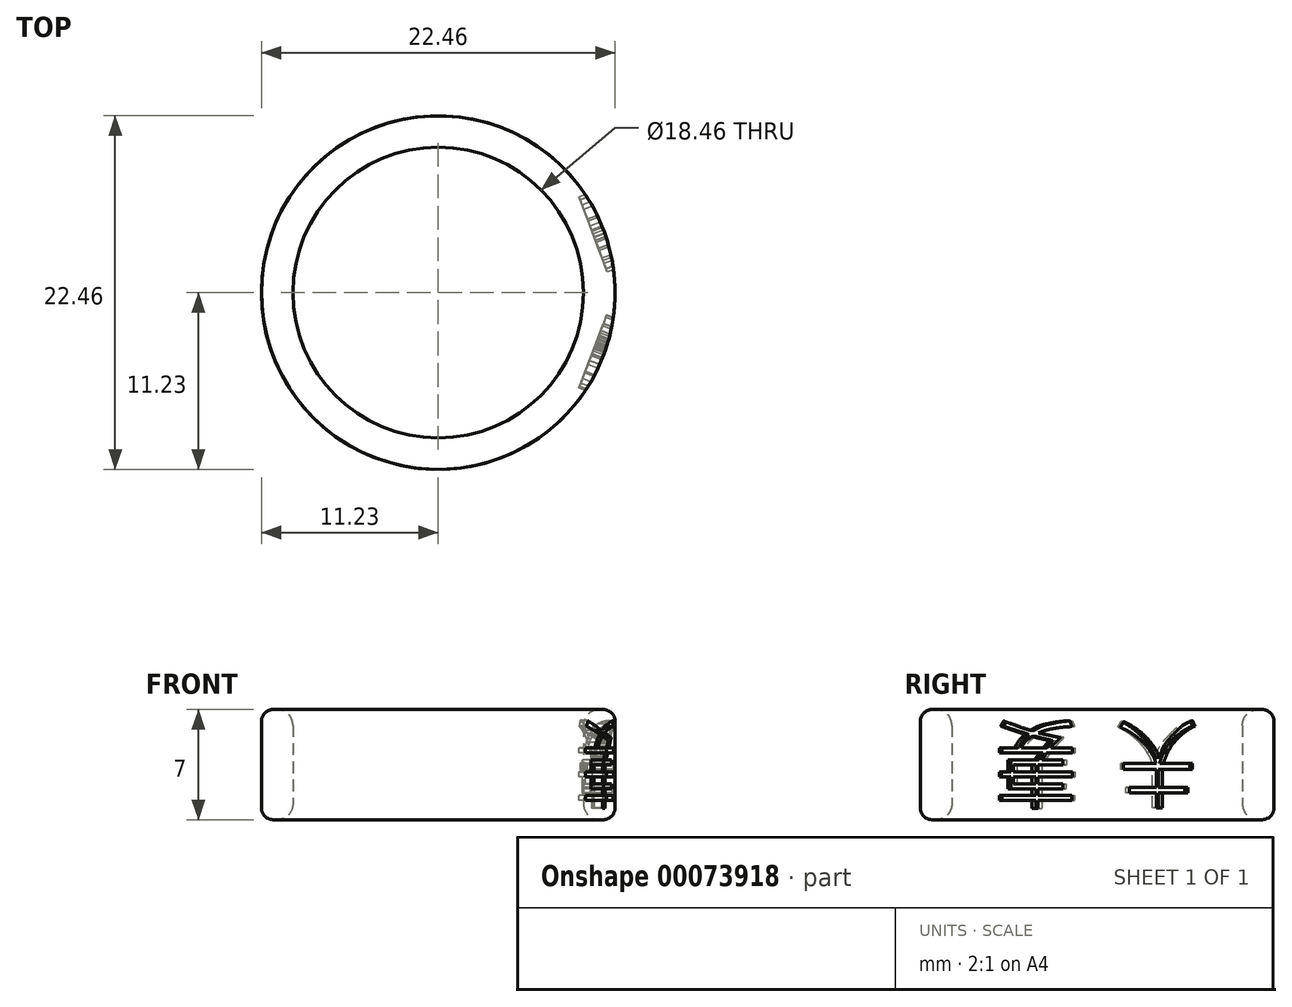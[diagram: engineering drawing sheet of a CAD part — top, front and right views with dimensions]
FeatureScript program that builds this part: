
annotation { "Feature Type Name" : "Feature", "Feature Type Description" : "" }
export const myFeature = defineFeature(function(context is Context, id is Id, definition is map)
    precondition{}
    {
        {
            var Q0;
            Q0=qCreatedBy(makeId("Top.planeOp"),FACE);
            var sketch = newSketch(context, id + "F0", { "sketchPlane" : qUnion([Q0])});
            skCircle(sketch, "E0", {"center": v(0, 0) * mm, "radius": 9.23 * mm});
            skCircle(sketch, "E1", {"center": v(0, 0) * mm, "radius": 11.23 * mm});
            skLineSegment(sketch, "E2", {"start": v(-11.23, 0) * mm, "end": v(11.23, 0) * mm, "construction": true});
            skSolve(sketch);
        }
        {
            var Q0;
            Q0 = qSketchRegion(id + "F0", true);
            extrude(context, id + "F1", {"entities" : qUnion([Q0]), "depth" : 7 * mm});
        }
        {
            var Q0;
            Q0=qCreatedBy(makeId("Front.planeOp"),FACE);
            var sketch = newSketch(context, id + "F2", { "sketchPlane" : qUnion([Q0])});
            skLineSegment(sketch, "E3", {"start": v(0, 0) * mm, "end": v(0, 6) * mm, "construction": true});
            skLineSegment(sketch, "E4", {"start": v(0, 3) * mm, "end": v(10.23, 3) * mm, "construction": true});
            skLineSegment(sketch, "E5", {"start": v(10.23, 3) * mm, "end": v(10.23, 4.75) * mm, "construction": true});
            skLineSegment(sketch, "E6", {"start": v(10.23, 3) * mm, "end": v(10.23, 1.25) * mm, "construction": true});
            skLineSegment(sketch, "E7", {"start": v(10.23, 4.75) * mm, "end": v(9.93, 4.75) * mm});
            skLineSegment(sketch, "E8", {"start": v(9.93, 4.75) * mm, "end": v(9.93, 5.25) * mm});
            skLineSegment(sketch, "E9", {"start": v(9.93, 5.25) * mm, "end": v(10.23, 5.25) * mm});
            skLineSegment(sketch, "E10", {"start": v(10.23, 5.25) * mm, "end": v(10.23, 4.75) * mm});
            skLineSegment(sketch, "E11", {"start": v(10.23, 1.25) * mm, "end": v(10.23, 0.75) * mm});
            skLineSegment(sketch, "E12", {"start": v(10.23, 0.75) * mm, "end": v(9.93, 0.75) * mm});
            skLineSegment(sketch, "E13", {"start": v(9.93, 0.75) * mm, "end": v(9.93, 1.25) * mm});
            skLineSegment(sketch, "E14", {"start": v(9.93, 1.25) * mm, "end": v(10.23, 1.25) * mm});
            skSolve(sketch);
        }
        {
            var Q0;
            Q0=makeQuery(id+"F1.opExtrude","CAP_EDGE",EDGE,{"disambiguationData":[OSD([sQuery(id+"F0.wireOp",EDGE,"E1")])],"isStart":false});
            var Q1;
            Q1=makeQuery(id+"F1.opExtrude","CAP_EDGE",EDGE,{"disambiguationData":[OSD([sQuery(id+"F0.wireOp",EDGE,"E1")])],"isStart":true});
            fillet(context, id + "F3", {"entities" : qUnion([Q0, Q1]), "radius" : .75 * mm, "tangentPropagation" : true, "allowEdgeOverflow" : false});
        }
        {
            var Q0;
            Q0=makeQuery(id+"F1.opExtrude","CAP_EDGE",EDGE,{"disambiguationData":[OSD([sQuery(id+"F0.wireOp",EDGE,"E0")])],"isStart":false});
            var Q1;
            Q1=makeQuery(id+"F1.opExtrude","CAP_EDGE",EDGE,{"disambiguationData":[OSD([sQuery(id+"F0.wireOp",EDGE,"E0")])],"isStart":true});
            fillet(context, id + "F4", {"entities" : qUnion([Q0, Q1]), "radius" : 1 * mm, "tangentPropagation" : true, "allowEdgeOverflow" : false});
        }
        {
            var Q0;
            Q0=sQuery(id+"F0.wireOp",VERTEX,"E2.end");
            var Q1;
            Q1=qCreatedBy(makeId("Right.planeOp"),FACE);
            cPlane(context, id + "F5", {"entities" : qUnion([Q0, Q1]), "cplaneType" : CPlaneType.PLANE_POINT, "offset" : 25 * mm, "width" : 150 * mm, "height" : 150 * mm});
        }
        {
            var Q0;
            Q0=qCreatedBy(makeId("Top.planeOp"),FACE);
            var sketch = newSketch(context, id + "F6", { "sketchPlane" : qUnion([Q0])});
            skCircle(sketch, "E15.0", {"center": v(0, 0) * mm, "radius": 11.23 * mm, "construction": true});
            skLineSegment(sketch, "E16", {"start": v(0, 11.23) * mm, "end": v(7, 11.23) * mm, "construction": true});
            skLineSegment(sketch, "E17", {"start": v(0, -11.23) * mm, "end": v(7, -11.23) * mm, "construction": true});
            skLineSegment(sketch, "E18", {"start": v(7, -11.23) * mm, "end": v(11.23, 0) * mm, "construction": true});
            skLineSegment(sketch, "E19", {"start": v(11.23, 0) * mm, "end": v(7, 11.23) * mm, "construction": true});
            skLineSegment(sketch, "E20.0", {"start": v(12.19, 0.29) * mm, "end": v(7.66, 12.3) * mm, "construction": true});
            skLineSegment(sketch, "E21.0", {"start": v(7.94, -11.58) * mm, "end": v(12.46, 0.44) * mm, "construction": true});
            skSolve(sketch);
        }
        {
            var Q0;
            Q0=sQuery(id+"F6.wireOp",EDGE,"E21.0");
            cPlane(context, id + "F7", {"entities" : qUnion([Q0]), "cplaneType" : CPlaneType.LINE_ANGLE, "offset" : 25 * mm, "angle" : 90 * degree, "width" : 150 * mm, "height" : 150 * mm});
        }
        {
            var Q0;
            Q0=sQuery(id+"F6.wireOp",EDGE,"E20.0");
            cPlane(context, id + "F8", {"entities" : qUnion([Q0]), "cplaneType" : CPlaneType.LINE_ANGLE, "offset" : 25 * mm, "angle" : 90 * degree, "width" : 150 * mm, "height" : 150 * mm});
        }
        {
            var Q0;
            Q0=qCreatedBy(id+"F8.planeOp",FACE);
            var sketch = newSketch(context, id + "F9", { "sketchPlane" : qUnion([Q0])});
            skFitSpline(sketch, "E22", {"points": [v(-2.32, 6.24) * mm, v(-2.09, 6.13) * mm, v(-1.85, 6) * mm, v(-1.62, 5.83) * mm]});
            skFitSpline(sketch, "E23", {"points": [v(-1.62, 5.83) * mm, v(-1.39, 5.68) * mm, v(-1.17, 5.5) * mm, v(-0.96, 5.3) * mm]});
            skFitSpline(sketch, "E24", {"points": [v(-0.96, 5.3) * mm, v(-0.76, 5.1) * mm, v(-0.57, 4.9) * mm, v(-0.4, 4.67) * mm]});
            skFitSpline(sketch, "E25", {"points": [v(-0.4, 4.67) * mm, v(-0.23, 4.45) * mm, v(-0.1, 4.2) * mm, v(0.01, 3.96) * mm]});
            skFitSpline(sketch, "E26", {"points": [v(0.01, 3.96) * mm, v(0.2, 4.47) * mm, v(0.49, 4.93) * mm, v(0.89, 5.33) * mm]});
            skFitSpline(sketch, "E27", {"points": [v(0.89, 5.33) * mm, v(1.29, 5.73) * mm, v(1.77, 6.05) * mm, v(2.33, 6.3) * mm]});
            skLineSegment(sketch, "E28", {"start": v(2.33, 6.3) * mm, "end": v(2.53, 5.94) * mm});
            skFitSpline(sketch, "E29", {"points": [v(2.53, 5.94) * mm, v(2.21, 5.82) * mm, v(1.92, 5.67) * mm, v(1.68, 5.5) * mm]});
            skFitSpline(sketch, "E30", {"points": [v(1.68, 5.5) * mm, v(1.42, 5.32) * mm, v(1.2, 5.12) * mm, v(1.02, 4.92) * mm]});
            skFitSpline(sketch, "E31", {"points": [v(1.02, 4.92) * mm, v(0.84, 4.72) * mm, v(0.68, 4.5) * mm, v(0.56, 4.26) * mm]});
            skFitSpline(sketch, "E32", {"points": [v(0.56, 4.26) * mm, v(0.44, 4.03) * mm, v(0.35, 3.8) * mm, v(0.29, 3.56) * mm]});
            skLineSegment(sketch, "E33", {"start": v(0.29, 3.56) * mm, "end": v(2.33, 3.56) * mm});
            skLineSegment(sketch, "E34", {"start": v(2.33, 3.56) * mm, "end": v(2.33, 3.2) * mm});
            skLineSegment(sketch, "E35", {"start": v(2.33, 3.2) * mm, "end": v(0.2, 3.2) * mm});
            skLineSegment(sketch, "E36", {"start": v(0.2, 3.2) * mm, "end": v(0.2, 2.07) * mm});
            skLineSegment(sketch, "E37", {"start": v(0.2, 2.07) * mm, "end": v(1.99, 2.07) * mm});
            skLineSegment(sketch, "E38", {"start": v(1.99, 2.07) * mm, "end": v(1.99, 1.72) * mm});
            skLineSegment(sketch, "E39", {"start": v(1.99, 1.72) * mm, "end": v(0.2, 1.72) * mm});
            skLineSegment(sketch, "E40", {"start": v(0.2, 1.72) * mm, "end": v(0.2, 0.76) * mm});
            skLineSegment(sketch, "E41", {"start": v(0.2, 0.76) * mm, "end": v(-0.2, 0.76) * mm});
            skLineSegment(sketch, "E42", {"start": v(-0.2, 0.76) * mm, "end": v(-0.2, 1.72) * mm});
            skLineSegment(sketch, "E43", {"start": v(-0.2, 1.72) * mm, "end": v(-1.99, 1.72) * mm});
            skLineSegment(sketch, "E44", {"start": v(-1.99, 1.72) * mm, "end": v(-1.99, 2.07) * mm});
            skLineSegment(sketch, "E45", {"start": v(-1.99, 2.07) * mm, "end": v(-0.2, 2.07) * mm});
            skLineSegment(sketch, "E46", {"start": v(-0.2, 2.07) * mm, "end": v(-0.2, 3.2) * mm});
            skLineSegment(sketch, "E47", {"start": v(-0.2, 3.2) * mm, "end": v(-2.35, 3.2) * mm});
            skLineSegment(sketch, "E48", {"start": v(-2.35, 3.2) * mm, "end": v(-2.35, 3.56) * mm});
            skLineSegment(sketch, "E49", {"start": v(-2.35, 3.56) * mm, "end": v(-0.22, 3.56) * mm});
            skFitSpline(sketch, "E50", {"points": [v(-0.22, 3.56) * mm, v(-0.3, 3.81) * mm, v(-0.42, 4.05) * mm, v(-0.57, 4.28) * mm]});
            skFitSpline(sketch, "E51", {"points": [v(-0.57, 4.28) * mm, v(-0.72, 4.5) * mm, v(-0.9, 4.72) * mm, v(-1.1, 4.92) * mm]});
            skFitSpline(sketch, "E52", {"points": [v(-1.1, 4.92) * mm, v(-1.31, 5.11) * mm, v(-1.54, 5.3) * mm, v(-1.78, 5.46) * mm]});
            skFitSpline(sketch, "E53", {"points": [v(-1.78, 5.46) * mm, v(-2.03, 5.62) * mm, v(-2.28, 5.76) * mm, v(-2.55, 5.87) * mm]});
            skLineSegment(sketch, "E54", {"start": v(-2.55, 5.87) * mm, "end": v(-2.32, 6.24) * mm});
            skLineSegment(sketch, "E55.0", {"start": v(-10.48, 7) * mm, "end": v(10.48, 7) * mm, "construction": true});
            skLineSegment(sketch, "E56", {"start": v(0, 0) * mm, "end": v(0, 7) * mm, "construction": true});
            skLineSegment(sketch, "E57", {"start": v(-2.32, 6.24) * mm, "end": v(2.33, 6.24) * mm, "construction": true});
            skLineSegment(sketch, "E58", {"start": v(0, 1.26) * mm, "end": v(0, 6.75) * mm, "construction": true});
            skLineSegment(sketch, "E59", {"start": v(0, 3.5) * mm, "end": v(2.33, 3.5) * mm, "construction": true});
            skLineSegment(sketch, "E60", {"start": v(0, 3.5) * mm, "end": v(0.82, 3.5) * mm, "construction": true});
            skSolve(sketch);
        }
        {
            var Q0;
            Q0=qCreatedBy(id+"F7.planeOp",FACE);
            var sketch = newSketch(context, id + "F10", { "sketchPlane" : qUnion([Q0])});
            skLineSegment(sketch, "E61.0", {"start": v(-10.48, 7) * mm, "end": v(10.48, 7) * mm, "construction": true});
            skLineSegment(sketch, "E62", {"start": v(0, 0) * mm, "end": v(0, 7) * mm, "construction": true});
            skLineSegment(sketch, "E63", {"start": v(0, 3.5) * mm, "end": v(-0.62, 3.5) * mm, "construction": true});
            skPoint(sketch, "E63.endSnap0", {"position": v(0, 3) * mm});
            skFitSpline(sketch, "E64", {"points": [v(-2.2, 6.27) * mm, v(-1.85, 6.15) * mm, v(-1.52, 6.04) * mm, v(-1.21, 5.94) * mm]});
            skFitSpline(sketch, "E65", {"points": [v(-1.21, 5.94) * mm, v(-0.9, 5.84) * mm, v(-0.6, 5.75) * mm, v(-0.3, 5.67) * mm]});
            skFitSpline(sketch, "E66", {"points": [v(-0.3, 5.67) * mm, v(0.03, 5.86) * mm, v(0.41, 6) * mm, v(0.84, 6.09) * mm]});
            skFitSpline(sketch, "E67", {"points": [v(0.84, 6.09) * mm, v(1.26, 6.18) * mm, v(1.74, 6.25) * mm, v(2.28, 6.29) * mm]});
            skLineSegment(sketch, "E68", {"start": v(2.28, 6.29) * mm, "end": v(2.42, 5.91) * mm});
            skFitSpline(sketch, "E69", {"points": [v(2.42, 5.91) * mm, v(1.98, 5.9) * mm, v(1.58, 5.85) * mm, v(1.22, 5.78) * mm]});
            skFitSpline(sketch, "E70", {"points": [v(1.22, 5.78) * mm, v(0.86, 5.72) * mm, v(0.54, 5.63) * mm, v(0.26, 5.51) * mm]});
            skFitSpline(sketch, "E71", {"points": [v(0.26, 5.51) * mm, v(0.5, 5.45) * mm, v(0.73, 5.4) * mm, v(0.96, 5.36) * mm]});
            skFitSpline(sketch, "E72", {"points": [v(0.96, 5.36) * mm, v(1.2, 5.3) * mm, v(1.45, 5.26) * mm, v(1.7, 5.22) * mm]});
            skFitSpline(sketch, "E73", {"points": [v(1.7, 5.22) * mm, v(1.6, 5.12) * mm, v(1.48, 5) * mm, v(1.37, 4.9) * mm]});
            skFitSpline(sketch, "E74", {"points": [v(1.37, 4.9) * mm, v(1.27, 4.8) * mm, v(1.16, 4.67) * mm, v(1.06, 4.55) * mm]});
            skLineSegment(sketch, "E75", {"start": v(1.06, 4.55) * mm, "end": v(2.43, 4.55) * mm});
            skLineSegment(sketch, "E76", {"start": v(2.43, 4.55) * mm, "end": v(2.43, 4.23) * mm});
            skLineSegment(sketch, "E77", {"start": v(2.43, 4.23) * mm, "end": v(0.8, 4.23) * mm});
            skFitSpline(sketch, "E78", {"points": [v(0.8, 4.23) * mm, v(0.74, 4.16) * mm, v(0.68, 4.1) * mm, v(0.63, 4.02) * mm]});
            skFitSpline(sketch, "E79", {"points": [v(0.63, 4.02) * mm, v(0.58, 3.95) * mm, v(0.54, 3.88) * mm, v(0.5, 3.8) * mm]});
            skLineSegment(sketch, "E80", {"start": v(0.5, 3.8) * mm, "end": v(1.86, 3.8) * mm});
            skLineSegment(sketch, "E81", {"start": v(1.86, 3.8) * mm, "end": v(1.86, 3.5) * mm});
            skLineSegment(sketch, "E82", {"start": v(1.86, 3.5) * mm, "end": v(0.2, 3.5) * mm});
            skLineSegment(sketch, "E83", {"start": v(0.2, 3.5) * mm, "end": v(0.2, 3.03) * mm});
            skLineSegment(sketch, "E84", {"start": v(0.2, 3.03) * mm, "end": v(2.44, 3.03) * mm});
            skLineSegment(sketch, "E85", {"start": v(2.44, 3.03) * mm, "end": v(2.44, 2.72) * mm});
            skLineSegment(sketch, "E86", {"start": v(2.44, 2.72) * mm, "end": v(0.2, 2.72) * mm});
            skLineSegment(sketch, "E87", {"start": v(0.2, 2.72) * mm, "end": v(0.2, 2.27) * mm});
            skLineSegment(sketch, "E88", {"start": v(0.2, 2.27) * mm, "end": v(1.84, 2.27) * mm});
            skLineSegment(sketch, "E89", {"start": v(1.84, 2.27) * mm, "end": v(1.84, 1.96) * mm});
            skLineSegment(sketch, "E90", {"start": v(1.84, 1.96) * mm, "end": v(0.2, 1.96) * mm});
            skLineSegment(sketch, "E91", {"start": v(0.2, 1.96) * mm, "end": v(0.2, 1.54) * mm});
            skLineSegment(sketch, "E92", {"start": v(0.2, 1.54) * mm, "end": v(2.42, 1.54) * mm});
            skLineSegment(sketch, "E93", {"start": v(2.42, 1.54) * mm, "end": v(2.42, 1.21) * mm});
            skLineSegment(sketch, "E94", {"start": v(2.42, 1.21) * mm, "end": v(0.2, 1.21) * mm});
            skLineSegment(sketch, "E95", {"start": v(0.2, 1.21) * mm, "end": v(0.2, 0.7) * mm});
            skLineSegment(sketch, "E96", {"start": v(0.2, 0.7) * mm, "end": v(-0.21, 0.7) * mm});
            skLineSegment(sketch, "E97", {"start": v(-0.21, 0.7) * mm, "end": v(-0.21, 1.21) * mm});
            skLineSegment(sketch, "E98", {"start": v(-0.21, 1.21) * mm, "end": v(-2.5, 1.21) * mm});
            skLineSegment(sketch, "E99", {"start": v(-2.5, 1.21) * mm, "end": v(-2.5, 1.54) * mm});
            skLineSegment(sketch, "E100", {"start": v(-2.5, 1.54) * mm, "end": v(-0.21, 1.54) * mm});
            skLineSegment(sketch, "E101", {"start": v(-0.21, 1.54) * mm, "end": v(-0.21, 1.96) * mm});
            skLineSegment(sketch, "E102", {"start": v(-0.21, 1.96) * mm, "end": v(-1.89, 1.96) * mm});
            skLineSegment(sketch, "E103", {"start": v(-1.89, 1.96) * mm, "end": v(-1.89, 2.72) * mm});
            skLineSegment(sketch, "E104", {"start": v(-1.89, 2.72) * mm, "end": v(-2.52, 2.72) * mm});
            skLineSegment(sketch, "E105", {"start": v(-2.52, 2.72) * mm, "end": v(-2.52, 3.03) * mm});
            skLineSegment(sketch, "E106", {"start": v(-2.52, 3.03) * mm, "end": v(-1.89, 3.03) * mm});
            skLineSegment(sketch, "E107", {"start": v(-1.89, 3.03) * mm, "end": v(-1.89, 3.8) * mm});
            skLineSegment(sketch, "E108", {"start": v(-1.89, 3.8) * mm, "end": v(0, 3.8) * mm});
            skFitSpline(sketch, "E109", {"points": [v(0, 3.8) * mm, v(0.04, 3.88) * mm, v(0.09, 3.95) * mm, v(0.14, 4.02) * mm]});
            skFitSpline(sketch, "E110", {"points": [v(0.14, 4.02) * mm, v(0.19, 4.1) * mm, v(0.24, 4.16) * mm, v(0.3, 4.23) * mm]});
            skLineSegment(sketch, "E111", {"start": v(0.3, 4.23) * mm, "end": v(-2.51, 4.23) * mm});
            skLineSegment(sketch, "E112", {"start": v(-2.51, 4.23) * mm, "end": v(-2.51, 4.55) * mm});
            skLineSegment(sketch, "E113", {"start": v(-2.51, 4.55) * mm, "end": v(-1.4, 4.55) * mm});
            skFitSpline(sketch, "E114", {"points": [v(-1.4, 4.55) * mm, v(-1.18, 4.9) * mm, v(-0.94, 5.2) * mm, v(-0.66, 5.42) * mm]});
            skFitSpline(sketch, "E115", {"points": [v(-0.66, 5.42) * mm, v(-0.93, 5.5) * mm, v(-1.2, 5.57) * mm, v(-1.49, 5.66) * mm]});
            skFitSpline(sketch, "E116", {"points": [v(-1.49, 5.66) * mm, v(-1.78, 5.75) * mm, v(-2.09, 5.84) * mm, v(-2.4, 5.95) * mm]});
            skLineSegment(sketch, "E117", {"start": v(-2.4, 5.95) * mm, "end": v(-2.2, 6.27) * mm});
            skFitSpline(sketch, "E118", {"points": [v(0.96, 5.03) * mm, v(0.78, 5.06) * mm, v(0.6, 5.1) * mm, v(0.4, 5.14) * mm]});
            skFitSpline(sketch, "E119", {"points": [v(0.4, 5.14) * mm, v(0.21, 5.19) * mm, v(0.02, 5.23) * mm, v(-0.18, 5.29) * mm]});
            skFitSpline(sketch, "E120", {"points": [v(-0.18, 5.29) * mm, v(-0.5, 5.09) * mm, v(-0.75, 4.84) * mm, v(-0.93, 4.55) * mm]});
            skLineSegment(sketch, "E121", {"start": v(-0.93, 4.55) * mm, "end": v(0.55, 4.55) * mm});
            skFitSpline(sketch, "E122", {"points": [v(0.55, 4.55) * mm, v(0.62, 4.64) * mm, v(0.7, 4.72) * mm, v(0.76, 4.8) * mm]});
            skFitSpline(sketch, "E123", {"points": [v(0.76, 4.8) * mm, v(0.83, 4.88) * mm, v(0.9, 4.96) * mm, v(0.96, 5.03) * mm]});
            skLineSegment(sketch, "E124", {"start": v(-1.48, 3.5) * mm, "end": v(-1.48, 3.03) * mm});
            skLineSegment(sketch, "E125", {"start": v(-1.48, 3.03) * mm, "end": v(-0.21, 3.03) * mm});
            skLineSegment(sketch, "E126", {"start": v(-0.21, 3.03) * mm, "end": v(-0.21, 3.5) * mm});
            skLineSegment(sketch, "E127", {"start": v(-0.21, 3.5) * mm, "end": v(-1.48, 3.5) * mm});
            skLineSegment(sketch, "E128", {"start": v(-0.21, 2.27) * mm, "end": v(-0.21, 2.72) * mm});
            skLineSegment(sketch, "E129", {"start": v(-0.21, 2.72) * mm, "end": v(-1.48, 2.72) * mm});
            skLineSegment(sketch, "E130", {"start": v(-1.48, 2.72) * mm, "end": v(-1.48, 2.27) * mm});
            skLineSegment(sketch, "E131", {"start": v(-1.48, 2.27) * mm, "end": v(-0.21, 2.27) * mm});
            skLineSegment(sketch, "E132", {"start": v(2.28, 6.29) * mm, "end": v(-2.2, 6.27) * mm, "construction": true});
            skLineSegment(sketch, "E133", {"start": v(0, 0.7) * mm, "end": v(0, 6.28) * mm, "construction": true});
            skLineSegment(sketch, "E134", {"start": v(0, 3.5) * mm, "end": v(0.2, 3.5) * mm, "construction": true});
            skSolve(sketch);
        }
        {
            var Q0;
            Q0 = qSketchRegion(id + "F10", true);
            extrude(context, id + "F11", {"entities" : qUnion([Q0]), "operationType" : NewBodyOperationType.REMOVE, "depth" : 1 * mm, "hasSecondDirection" : true, "secondDirectionOppositeDirection" : true, "secondDirectionDepth" : 1 * mm});
        }
        {
            var Q0;
            Q0 = qSketchRegion(id + "F9", true);
            extrude(context, id + "F12", {"entities" : qUnion([Q0]), "operationType" : NewBodyOperationType.REMOVE, "depth" : 1 * mm, "hasSecondDirection" : true, "secondDirectionOppositeDirection" : true, "secondDirectionDepth" : 1 * mm});
        }
    });
